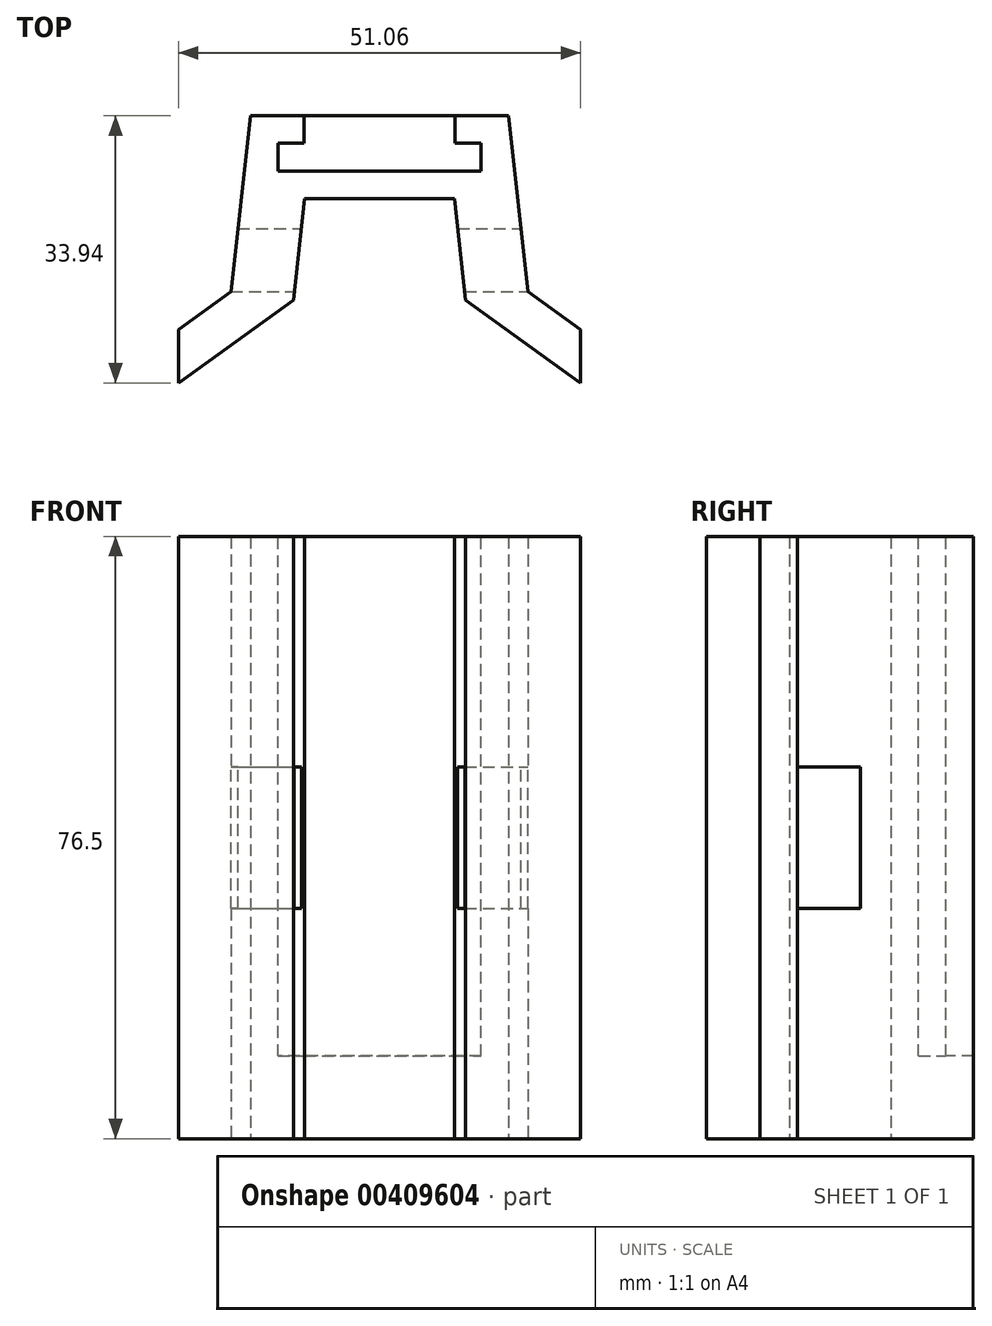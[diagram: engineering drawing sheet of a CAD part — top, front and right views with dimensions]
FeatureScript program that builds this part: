
annotation { "Feature Type Name" : "Feature", "Feature Type Description" : "" }
export const myFeature = defineFeature(function(context is Context, id is Id, definition is map)
    precondition{}
    {
        {
            var Q0;
            Q0=qCreatedBy(makeId("Top.planeOp"),FACE);
            var sketch = newSketch(context, id + "F0", { "sketchPlane" : qUnion([Q0])});
            skLineSegment(sketch, "E0", {"start": v(16.38, 0) * mm, "end": v(18.88, -22.36) * mm});
            skLineSegment(sketch, "E1", {"start": v(18.88, -22.36) * mm, "end": v(25.53, -27.16) * mm});
            skLineSegment(sketch, "E2", {"start": v(25.53, -27.16) * mm, "end": v(25.53, -33.94) * mm});
            skLineSegment(sketch, "E3", {"start": v(25.53, -33.94) * mm, "end": v(10.95, -23.42) * mm});
            skLineSegment(sketch, "E4", {"start": v(9.5, -10.5) * mm, "end": v(10.95, -23.42) * mm});
            skLineSegment(sketch, "E5", {"start": v(0, 0) * mm, "end": v(16.38, 0) * mm});
            skLineSegment(sketch, "E6", {"start": v(9.5, -10.5) * mm, "end": v(0, -10.5) * mm});
            skLineSegment(sketch, "E7.MirrorCS", {"start": v(-18.88, -22.36) * mm, "end": v(-25.53, -27.16) * mm});
            skLineSegment(sketch, "E8.MirrorCS", {"start": v(-25.53, -33.94) * mm, "end": v(-10.95, -23.42) * mm});
            skLineSegment(sketch, "E9.MirrorCS", {"start": v(-9.5, -10.5) * mm, "end": v(0, -10.5) * mm});
            skLineSegment(sketch, "E10.MirrorCS", {"start": v(-25.53, -27.16) * mm, "end": v(-25.53, -33.94) * mm});
            skLineSegment(sketch, "E11.MirrorCS", {"start": v(-16.38, 0) * mm, "end": v(-18.88, -22.36) * mm});
            skLineSegment(sketch, "E12.MirrorCS", {"start": v(-9.5, -10.5) * mm, "end": v(-10.95, -23.42) * mm});
            skLineSegment(sketch, "E13.MirrorCS", {"start": v(0, 0) * mm, "end": v(-16.38, 0) * mm});
            skSolve(sketch);
        }
        {
            var Q0;
            Q0 = qSketchRegion(id + "F0", true);
            extrude(context, id + "F1", {"entities" : qUnion([Q0]), "depth" : 76.5 * mm});
        }
        {
            var Q0;
            Q0=makeQuery(id+"F1.opExtrude","CAP_FACE",FACE,{"disambiguationData":[OSD([sQuery(id+"F0.wireOp",EDGE,"E0"),sQuery(id+"F0.wireOp",EDGE,"E1"),sQuery(id+"F0.wireOp",EDGE,"E2"),sQuery(id+"F0.wireOp",EDGE,"E3"),sQuery(id+"F0.wireOp",EDGE,"E4"),sQuery(id+"F0.wireOp",EDGE,"E5"),sQuery(id+"F0.wireOp",EDGE,"E6"),sQuery(id+"F0.wireOp",EDGE,"E7.MirrorCS"),sQuery(id+"F0.wireOp",EDGE,"E8.MirrorCS"),sQuery(id+"F0.wireOp",EDGE,"E9.MirrorCS"),sQuery(id+"F0.wireOp",EDGE,"E10.MirrorCS"),sQuery(id+"F0.wireOp",EDGE,"E11.MirrorCS"),sQuery(id+"F0.wireOp",EDGE,"E12.MirrorCS"),sQuery(id+"F0.wireOp",EDGE,"E13.MirrorCS")])],"isStart":false});
            var sketch = newSketch(context, id + "F2", { "sketchPlane" : qUnion([Q0])});
            skLineSegment(sketch, "E14", {"start": v(-9.6, 0) * mm, "end": v(9.6, 0) * mm});
            skLineSegment(sketch, "E15", {"start": v(9.6, 0) * mm, "end": v(9.6, -3.5) * mm});
            skLineSegment(sketch, "E16", {"start": v(9.6, -3.5) * mm, "end": v(12.9, -3.5) * mm});
            skLineSegment(sketch, "E17", {"start": v(12.9, -3.5) * mm, "end": v(12.9, -7) * mm});
            skLineSegment(sketch, "E18", {"start": v(12.9, -7) * mm, "end": v(-12.9, -7) * mm});
            skLineSegment(sketch, "E19", {"start": v(-12.9, -7) * mm, "end": v(-12.9, -3.5) * mm});
            skLineSegment(sketch, "E20", {"start": v(-12.9, -3.5) * mm, "end": v(-9.6, -3.5) * mm});
            skLineSegment(sketch, "E21", {"start": v(-9.6, -3.5) * mm, "end": v(-9.6, 0) * mm});
            skLineSegment(sketch, "E22", {"start": v(0, 0) * mm, "end": v(0, -10.5) * mm, "construction": true});
            skLineSegment(sketch, "E23", {"start": v(0, -7) * mm, "end": v(0, -4.27) * mm, "construction": true});
            skSolve(sketch);
        }
        {
            var Q0;
            Q0 = qSketchRegion(id + "F2", true);
            extrude(context, id + "F3", {"entities" : qUnion([Q0]), "operationType" : NewBodyOperationType.REMOVE, "oppositeDirection" : true, "depth" : 66 * mm});
        }
        {
            var Q0;
            Q0=qCreatedBy(makeId("Right.planeOp"),FACE);
            var Q1;
            Q1=makeQuery(id+"F1.opExtrude","CAP_VERTEX",VERTEX,{"disambiguationData":[OSD([sQuery(id+"F0.wireOp",EDGE,"E0"),sQuery(id+"F0.wireOp",EDGE,"E1")])],"isStart":true});
            cPlane(context, id + "F4", {"entities" : qUnion([Q0, Q1]), "cplaneType" : CPlaneType.PLANE_POINT, "offset" : 25 * mm, "width" : 150 * mm, "height" : 150 * mm});
        }
        {
            var Q0;
            Q0=qCreatedBy(id+"F4.planeOp",FACE);
            var sketch = newSketch(context, id + "F5", { "sketchPlane" : qUnion([Q0])});
            skPoint(sketch, "E24.0", {"position": v(-22.36, 38.25) * mm});
            skLineSegment(sketch, "E25.bottom", {"start": v(-14.36, 29.25) * mm, "end": v(-22.36, 29.25) * mm});
            skLineSegment(sketch, "E25.top", {"start": v(-14.36, 47.25) * mm, "end": v(-22.36, 47.25) * mm});
            skLineSegment(sketch, "E25.left", {"start": v(-14.36, 29.25) * mm, "end": v(-14.36, 47.25) * mm});
            skLineSegment(sketch, "E25.right", {"start": v(-22.36, 29.25) * mm, "end": v(-22.36, 47.25) * mm});
            skPoint(sketch, "E25.middle", {"position": v(-18.36, 38.25) * mm});
            skSolve(sketch);
        }
        {
            var Q0;
            Q0 = qSketchRegion(id + "F5", true);
            extrude(context, id + "F6", {"entities" : qUnion([Q0]), "operationType" : NewBodyOperationType.REMOVE, "endBound" : BoundingType.THROUGH_ALL, "oppositeDirection" : true, "depth" : 25 * mm});
        }
    });
